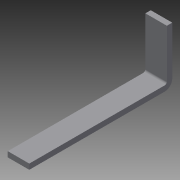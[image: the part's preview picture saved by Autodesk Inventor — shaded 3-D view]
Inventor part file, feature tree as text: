
AUTODESK INVENTOR PART (.ipt)
format: ipt  version: 2013 (Build 170138000, 138)  size: 91,648 bytes
history: native  units: in
note: dims shown in document units (in); Inventor stores cm internally (conversion verified against a paired STEP export)
features: sheet_metal_op x4, sketch x2, other x2
ambient origin geometry x8: Origin, YZ Plane, XZ Plane, XY Plane, X Axis, Y Axis, Z Axis, Center Point
bodies: Solid1 (feature_tree)
feature tree (8):
  sheet_metal_op  "Face1"
  sheet_metal_op  "Flange1"
  sketch  "Sketch1"  dims[d0=0.5in]
  other  "Plate1"
  sketch  "Sketch2"  dims[d1=1.125in d2=0.125in d3=0.125in d4=0.0625in d5=0.25in d6=0.125in d7=3.3222in d8=90.0deg d9=0.05in d10=0.5in d11=0.125in d12=0.125in]
  other  "Plate2"
  sheet_metal_op  "Bend1"
  sheet_metal_op  "Corner1"
